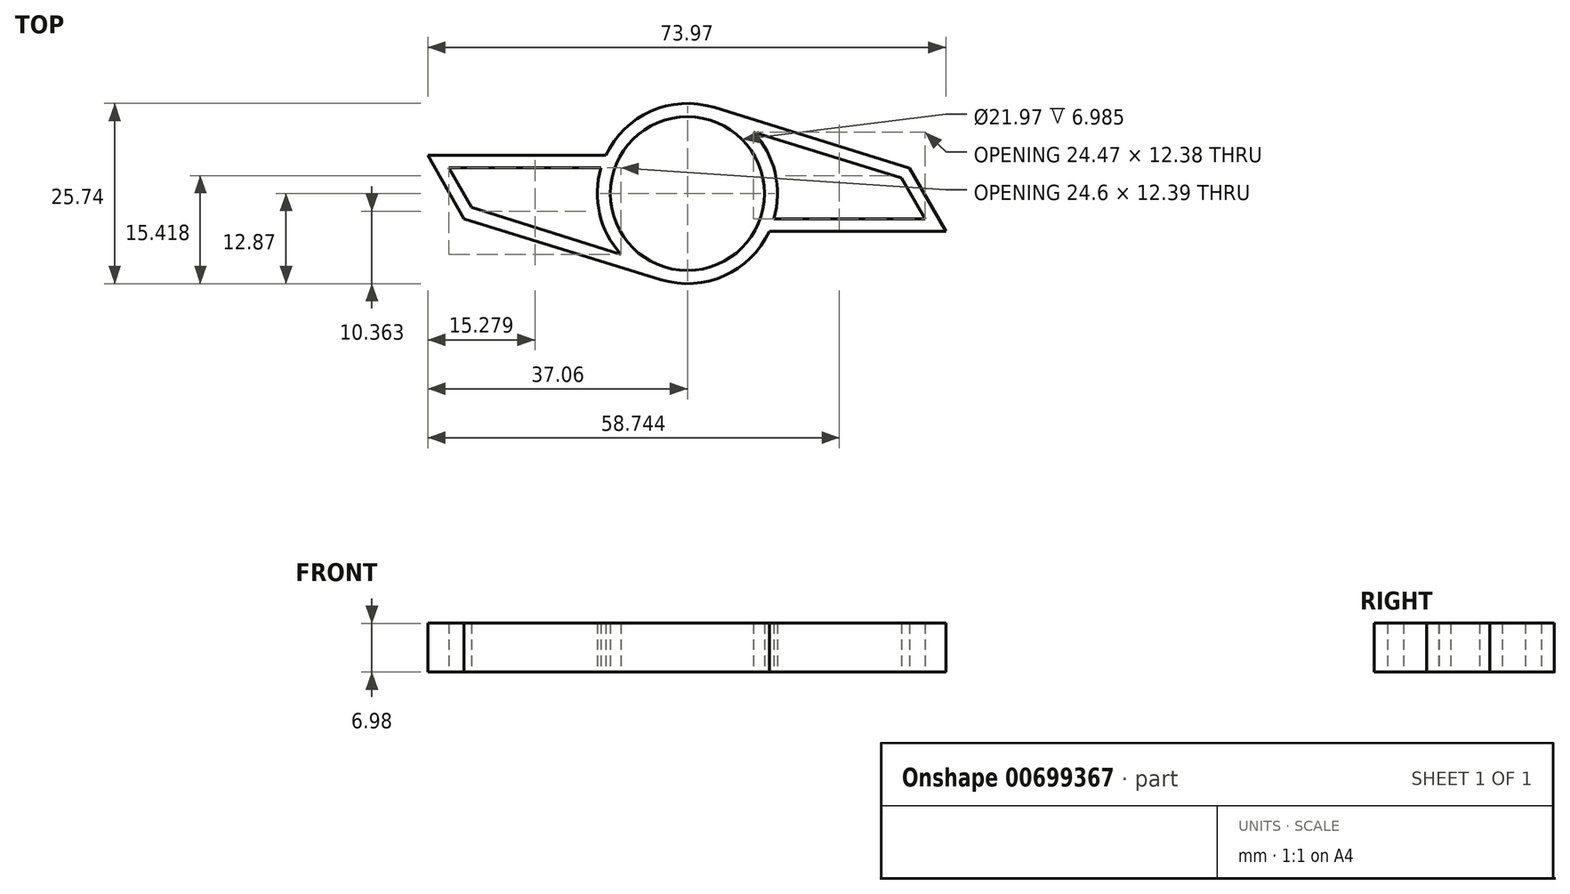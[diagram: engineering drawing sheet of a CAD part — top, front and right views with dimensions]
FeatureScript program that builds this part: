
annotation { "Feature Type Name" : "Feature", "Feature Type Description" : "" }
export const myFeature = defineFeature(function(context is Context, id is Id, definition is map)
    precondition{}
    {
        {
            var Q0;
            Q0=qCreatedBy(makeId("Top.planeOp"),FACE);
            var sketch = newSketch(context, id + "F0", { "sketchPlane" : qUnion([Q0])});
            skCircle(sketch, "E0", {"center": v(0, 0) * mm, "radius": 10.99 * mm});
            skCircle(sketch, "E1", {"center": v(0, 0) * mm, "radius": 12.87 * mm});
            skLineSegment(sketch, "E2", {"start": v(11.7, -5.37) * mm, "end": v(36.91, -5.37) * mm});
            skLineSegment(sketch, "E3", {"start": v(36.91, -5.37) * mm, "end": v(31.7, 3.65) * mm});
            skLineSegment(sketch, "E4", {"start": v(31.7, 3.65) * mm, "end": v(3.8, 12.3) * mm});
            skLineSegment(sketch, "E5", {"start": v(-11.66, 5.44) * mm, "end": v(-37.06, 5.44) * mm});
            skLineSegment(sketch, "E6", {"start": v(-37.06, 5.44) * mm, "end": v(-31.88, -3.6) * mm});
            skLineSegment(sketch, "E7", {"start": v(-31.88, -3.6) * mm, "end": v(-3.8, -12.3) * mm});
            skLineSegment(sketch, "E8", {"start": v(-34.08, 3.69) * mm, "end": v(-12.33, 3.69) * mm});
            skLineSegment(sketch, "E9", {"start": v(-34.08, 3.69) * mm, "end": v(-30.85, -1.94) * mm});
            skLineSegment(sketch, "E10", {"start": v(-30.85, -1.94) * mm, "end": v(-9.48, -8.7) * mm});
            skLineSegment(sketch, "E11", {"start": v(33.92, -3.64) * mm, "end": v(12.34, -3.64) * mm});
            skLineSegment(sketch, "E12", {"start": v(33.92, -3.64) * mm, "end": v(30.55, 2.2) * mm});
            skLineSegment(sketch, "E13", {"start": v(30.55, 2.2) * mm, "end": v(9.45, 8.74) * mm});
            skSolve(sketch);
        }
        {
            var Q0;
            Q0=qSketchRegion(id+"F0",true);
            extrude(context, id + "F1", {"entities" : qUnion([Q0]), "endBound" : BoundingType.SYMMETRIC, "depth" : 7 * mm, "offsetDistance" : 25.4 * mm});
        }
    });
